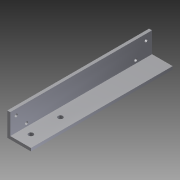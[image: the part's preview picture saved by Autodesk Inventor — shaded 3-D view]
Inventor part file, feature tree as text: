
AUTODESK INVENTOR PART (.ipt)
format: ipt  version: 2012 (Build 160160000, 160)  size: 104,960 bytes
history: native  units: in
note: dims shown in document units (in); Inventor stores cm internally (conversion verified against a paired STEP export)
features: extrude x3, sketch x3
ambient origin geometry x8: Origin, YZ Plane, XZ Plane, XY Plane, X Axis, Y Axis, Z Axis, Center Point
bodies: Solid1 (feature_tree)
feature tree (6):
  extrude  "Extrusion1"  Depth=1.0in
  extrude  "Extrusion4"  Depth=0.125in
  extrude  "Extrusion5"  Depth=0.5in
  sketch  "Sketch1"  dims[d0=1.0in d1=1.0in]
  sketch  "Sketch3"  dims[d2=0.125in d3=0.125in]
  sketch  "Sketch4"  dims[d4=6.0in d5=0.0in d20=0.5in d21=1.25in d22=0.2in d23=0.5in d24=1.0in d25=0.0in d26=0.25in d27=0.75in d28=0.125in d29=0.25in d30=0.6875in d31=1.0in d32=0.0in]
